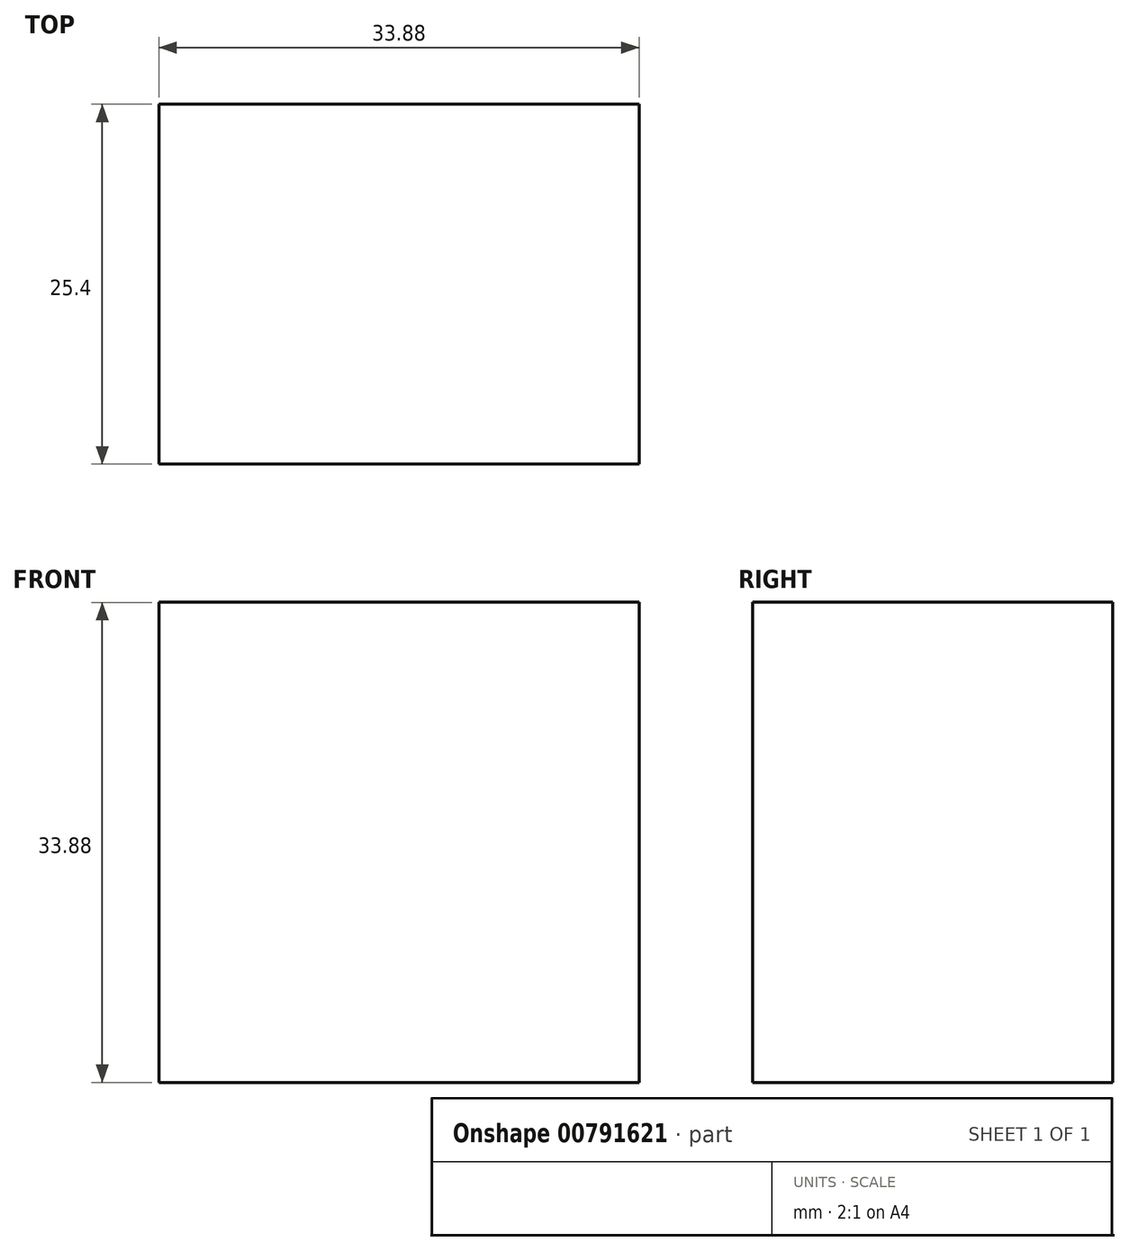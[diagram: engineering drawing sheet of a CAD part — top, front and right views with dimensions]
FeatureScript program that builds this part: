
annotation { "Feature Type Name" : "Feature", "Feature Type Description" : "" }
export const myFeature = defineFeature(function(context is Context, id is Id, definition is map)
    precondition{}
    {
        {
            var Q0;
            Q0=qCreatedBy(makeId("Front.planeOp"),FACE);
            var sketch = newSketch(context, id + "F0", { "sketchPlane" : qUnion([Q0])});
            skLineSegment(sketch, "E0", {"start": v(0, 0) * mm, "end": v(-33.88, 0) * mm});
            skLineSegment(sketch, "E1", {"start": v(-33.88, 33.88) * mm, "end": v(0, 33.88) * mm});
            skLineSegment(sketch, "E2", {"start": v(0, 33.88) * mm, "end": v(0, 0) * mm});
            skLineSegment(sketch, "E3", {"start": v(-33.88, 0) * mm, "end": v(-33.88, 33.88) * mm});
            skSolve(sketch);
        }
        {
            var Q0;
            Q0=sQuery(id+"F0.wireOp",EDGE,"E1");
            var Q1;
            Q1=sQuery(id+"F0.wireOp",EDGE,"E3");
            var Q2;
            Q2=sQuery(id+"F0.wireOp",EDGE,"E2");
            var Q3;
            Q3=sQuery(id+"F0.wireOp",EDGE,"E0");
            extrude(context, id + "F1", {"bodyType" : ToolBodyType.SURFACE, "surfaceEntities" : qUnion([Q0, Q1, Q2, Q3]), "depth" : 25.4 * mm, "offsetDistance" : 25.4 * mm});
        }
    });
